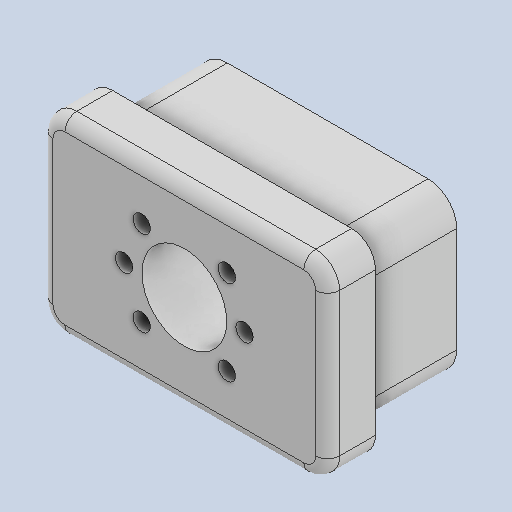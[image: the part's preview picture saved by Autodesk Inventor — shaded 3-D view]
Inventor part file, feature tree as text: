
AUTODESK INVENTOR PART (.ipt)
format: ipt  version: 2023 (Build 270158000, 158)  size: 219,136 bytes
history: native  units: in
note: dims shown in document units (in); Inventor stores cm internally (conversion verified against a paired STEP export)
features: extrude x3, sketch x3, fillet x1
ambient origin geometry x8: Origin, YZ Plane, XZ Plane, XY Plane, X Axis, Y Axis, Z Axis, Center Point
bodies: Solid1 (feature_tree)
feature tree (7):
  extrude  "Extrusion1"  Depth=1.7in
  extrude  "Extrusion2"  Depth=1.0in TaperAngle=0.0deg
  fillet  "Fillet1"  Radius=3.0in
  extrude  "Extrusion3"  Depth=0.25in
  sketch  "Sketch1"  dims[d0=2.7in d1=1.7in]
  sketch  "Sketch2"  dims[d3=0.3in d4=1.0in d5=0.0in d6=3.0in]
  sketch  "Sketch3"  dims[d7=2.0in d8=0.25in d9=0.5in d10=0.0in d11=0.125in d12=0.8858in d13=1.2598in d14=0.1811in d15=45.0deg d16=0.5in d17=0.0in]
